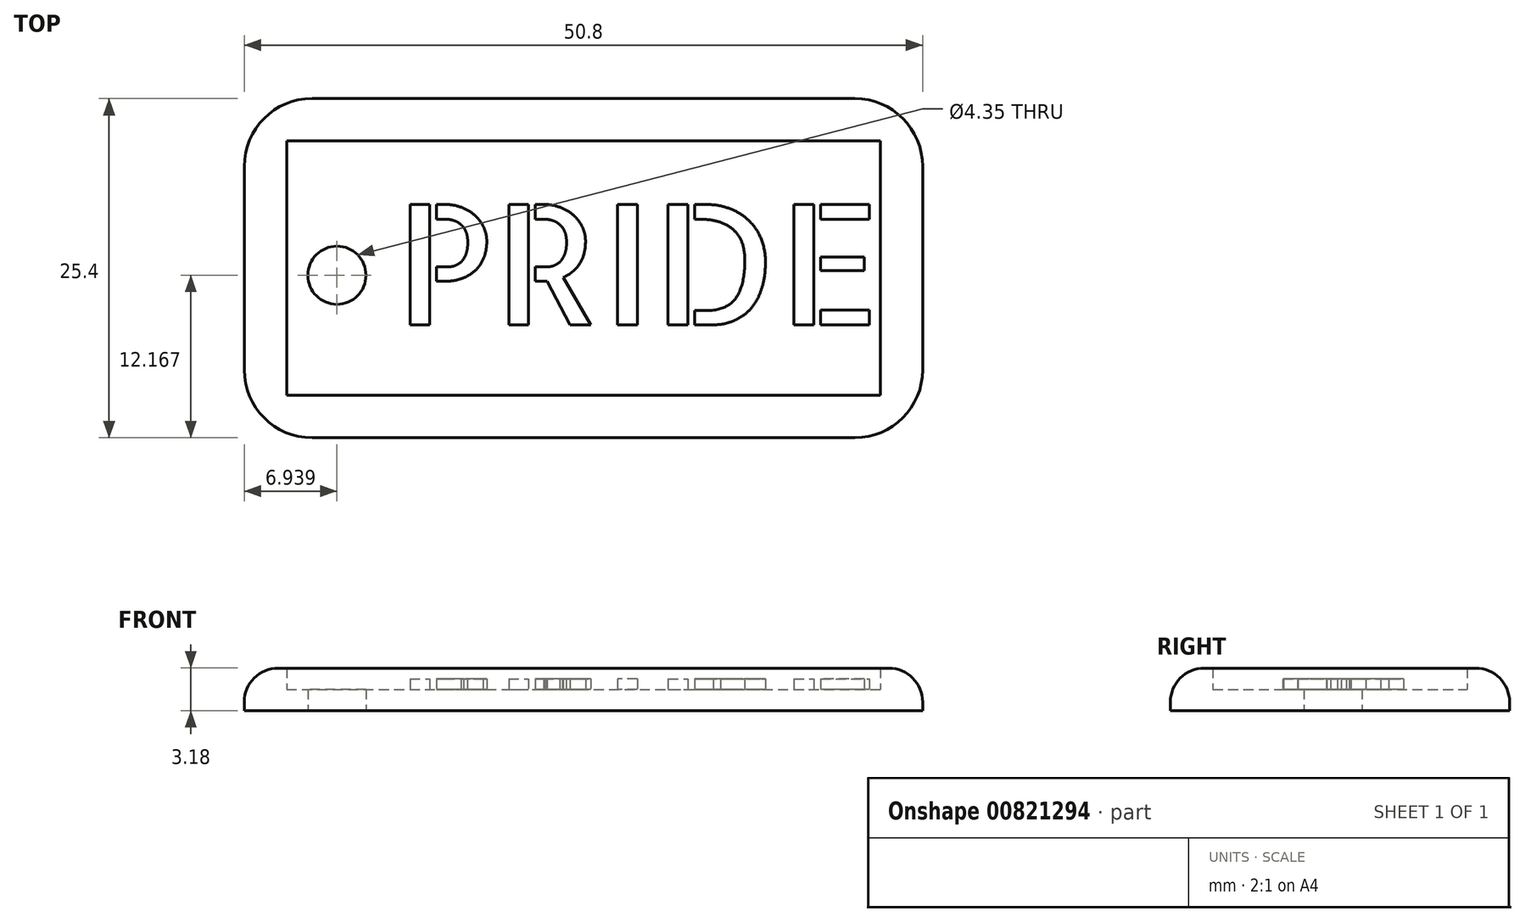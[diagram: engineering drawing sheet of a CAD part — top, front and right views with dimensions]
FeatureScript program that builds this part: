
annotation { "Feature Type Name" : "Feature", "Feature Type Description" : "" }
export const myFeature = defineFeature(function(context is Context, id is Id, definition is map)
    precondition{}
    {
        {
            var Q0;
            Q0=qCreatedBy(makeId("Top.planeOp"),FACE);
            var sketch = newSketch(context, id + "F0", { "sketchPlane" : qUnion([Q0])});
            skLineSegment(sketch, "E0.bottom", {"start": v(0, 0) * mm, "end": v(50.8, 0) * mm});
            skLineSegment(sketch, "E0.top", {"start": v(0, 25.4) * mm, "end": v(50.8, 25.4) * mm});
            skLineSegment(sketch, "E0.left", {"start": v(0, 0) * mm, "end": v(0, 25.4) * mm});
            skLineSegment(sketch, "E0.right", {"start": v(50.8, 0) * mm, "end": v(50.8, 25.4) * mm});
            skCircle(sketch, "E1", {"center": v(6.94, 12.17) * mm, "radius": 2.18 * mm});
            skLineSegment(sketch, "E2.0", {"start": v(3.17, 22.23) * mm, "end": v(47.62, 22.23) * mm});
            skLineSegment(sketch, "E2.1", {"start": v(3.17, 3.18) * mm, "end": v(3.17, 22.23) * mm});
            skLineSegment(sketch, "E2.2", {"start": v(3.17, 3.18) * mm, "end": v(47.62, 3.18) * mm});
            skLineSegment(sketch, "E2.3", {"start": v(47.62, 3.18) * mm, "end": v(47.62, 22.23) * mm});
            skSolve(sketch);
        }
        {
            var Q0;
            Q0=makeQuery(id+"F0.imprint","IMPRINT",FACE,{"disambiguationData":[TD([[makeQuery(id+"F0.imprint","IMPRINT",EDGE,{"derivedFrom":sQuery(id+"F0.wireOp",EDGE,"E1")}),-1.0]])]});
            extrude(context, id + "F1", {"entities" : qUnion([Q0]), "depth" : 1.59 * mm, "offsetDistance" : 25.4 * mm});
        }
        {
            var Q0;
            Q0 = qSketchRegion(id + "F0", true);
            extrude(context, id + "F2", {"entities" : qUnion([Q0]), "operationType" : NewBodyOperationType.ADD, "depth" : 3.17 * mm, "offsetDistance" : 25.4 * mm});
        }
        {
            var Q0;
            Q0=makeQuery(id+"F2.opExtrude","SWEPT_EDGE",EDGE,{"disambiguationData":[OSD([sQuery(id+"F0.wireOp",EDGE,"E0.bottom"),sQuery(id+"F0.wireOp",EDGE,"E0.right")])]});
            var Q1;
            Q1=makeQuery(id+"F2.opExtrude","SWEPT_EDGE",EDGE,{"disambiguationData":[OSD([sQuery(id+"F0.wireOp",EDGE,"E0.bottom"),sQuery(id+"F0.wireOp",EDGE,"E0.left")])]});
            var Q2;
            Q2=makeQuery(id+"F2.opExtrude","SWEPT_EDGE",EDGE,{"disambiguationData":[OSD([sQuery(id+"F0.wireOp",EDGE,"E0.top"),sQuery(id+"F0.wireOp",EDGE,"E0.right")])]});
            var Q3;
            Q3=makeQuery(id+"F2.opExtrude","SWEPT_EDGE",EDGE,{"disambiguationData":[OSD([sQuery(id+"F0.wireOp",EDGE,"E0.top"),sQuery(id+"F0.wireOp",EDGE,"E0.left")])]});
            fillet(context, id + "F3", {"entities" : qUnion([Q0, Q1, Q2, Q3]), "radius" : 5.08 * mm, "tangentPropagation" : true, "allowEdgeOverflow" : false});
        }
        {
            var Q0;
            Q0=makeQuery(id+"F2.opExtrude","CAP_EDGE",EDGE,{"disambiguationData":[OSD([sQuery(id+"F0.wireOp",EDGE,"E0.bottom")])],"isStart":false});
            fillet(context, id + "F4", {"entities" : qUnion([Q0]), "radius" : 2.54 * mm, "tangentPropagation" : true, "allowEdgeOverflow" : false});
        }
        {
            var Q0;
            Q0=makeQuery(id+"F1.opExtrude","CAP_FACE",FACE,{"disambiguationData":[OSD([sQuery(id+"F0.wireOp",EDGE,"E1"),sQuery(id+"F0.wireOp",EDGE,"E2.0"),sQuery(id+"F0.wireOp",EDGE,"E2.1"),sQuery(id+"F0.wireOp",EDGE,"E2.2"),sQuery(id+"F0.wireOp",EDGE,"E2.3")])],"isStart":false});
            var sketch = newSketch(context, id + "F5", { "sketchPlane" : qUnion([Q0])});
            skText(sketch, "E3", { "text": "PRIDE", "fontName": "AllertaStencil-Regular.ttf"});
            const initialGuessF5  = {"E3": [0.0113, 0.00845, 1, 0, 0.00903]};
            skSetInitialGuess(sketch, initialGuessF5);
            skSolve(sketch);
        }
        {
            var Q0;
            Q0 = qSketchRegion(id + "F5", true);
            extrude(context, id + "F6", {"entities" : qUnion([Q0]), "operationType" : NewBodyOperationType.ADD, "depth" : 0.8 * mm, "offsetDistance" : 25.4 * mm});
        }
    });
